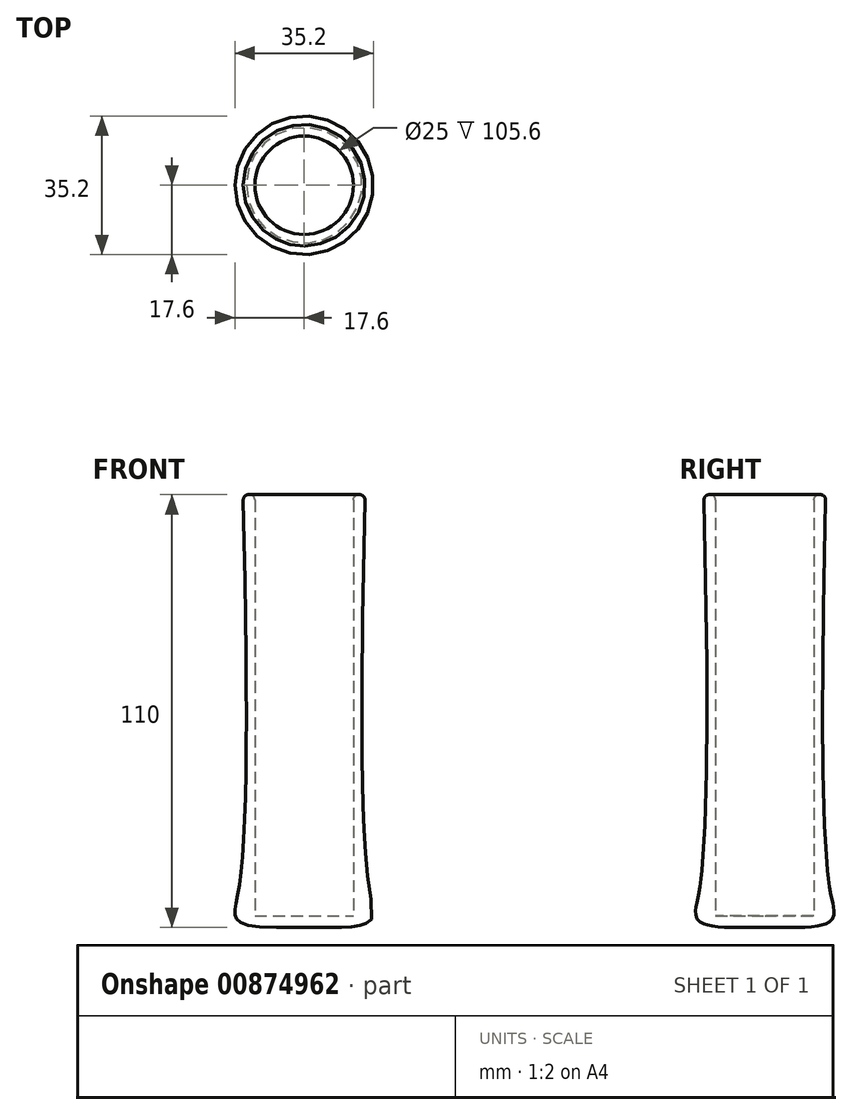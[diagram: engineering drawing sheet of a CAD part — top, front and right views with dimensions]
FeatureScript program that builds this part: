
annotation { "Feature Type Name" : "Feature", "Feature Type Description" : "" }
export const myFeature = defineFeature(function(context is Context, id is Id, definition is map)
    precondition{}
    {
        {
            var Q0;
            Q0=qCreatedBy(makeId("Front.planeOp"),FACE);
            var sketch = newSketch(context, id + "F0", { "sketchPlane" : qUnion([Q0])});
            skLineSegment(sketch, "E0.bottom", {"start": v(12.5, 110) * mm, "end": v(15.5, 110) * mm});
            skLineSegment(sketch, "E0.left", {"start": v(12.5, 110) * mm, "end": v(12.5, 3) * mm});
            skLineSegment(sketch, "E1.top", {"start": v(12.5, 3) * mm, "end": v(0, 3) * mm});
            skLineSegment(sketch, "E1.right", {"start": v(0, 0) * mm, "end": v(0, 3) * mm});
            skLineSegment(sketch, "E2", {"start": v(0, 0) * mm, "end": v(7.01, 0) * mm});
            skFitSpline(sketch, "E3", {"points": [v(7.01, 0) * mm, v(17.52, 3.04) * mm, v(16.58, 9.64) * mm, v(15.5, 110) * mm], "startDerivative": vector(115.4, 0) * mm, "endDerivative": vector(6.37, 248.35) * mm});
            skLineSegment(sketch, "E4", {"start": v(0, 0) * mm, "end": v(0, 115.85) * mm, "construction": true});
            skSolve(sketch);
        }
        {
            var Q0;
            Q0=makeQuery(id+"F0.imprint","IMPRINT",FACE,{"disambiguationData":[TD([[makeQuery(id+"F0.imprint","IMPRINT",EDGE,{"derivedFrom":sQuery(id+"F0.wireOp",EDGE,"E0.bottom")}),-1.0]])]});
            var Q1;
            Q1=sQuery(id+"F0.wireOp",EDGE,"E4");
            revolve(context, id + "F1", {"surfaceOperationType" : NewSurfaceOperationType.NEW, "entities" : qUnion([Q0]), "axis" : qUnion([Q1]), "revolveType" : RevolveType.FULL});
        }
        {
            var Q0;
            Q0=makeQuery(id+"F1.opRevolve","SWEPT_FACE",FACE,{"disambiguationData":[OSD([sQuery(id+"F0.wireOp",EDGE,"E0.bottom")])]});
            fillet(context, id + "F2", {"entities" : qUnion([Q0]), "radius" : 1.4 * mm, "tangentPropagation" : true, "allowEdgeOverflow" : false});
        }
    });
